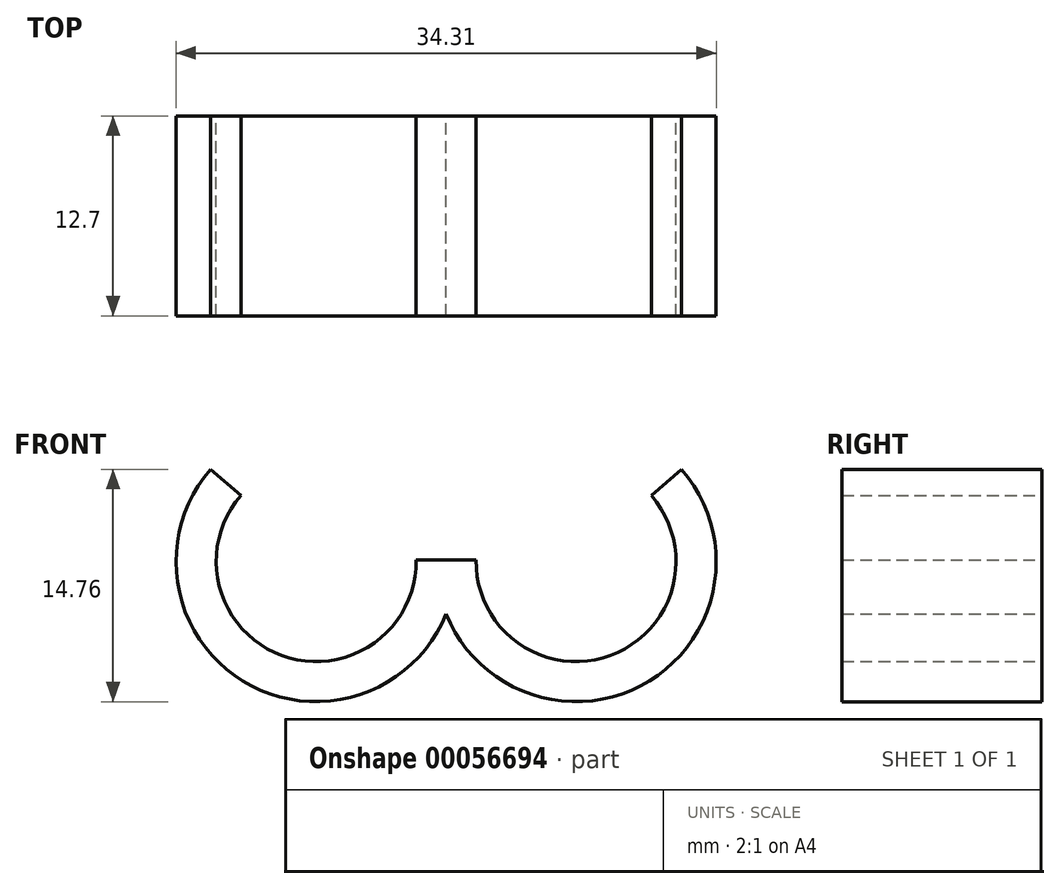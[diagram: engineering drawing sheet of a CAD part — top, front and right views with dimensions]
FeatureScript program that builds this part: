
annotation { "Feature Type Name" : "Feature", "Feature Type Description" : "" }
export const myFeature = defineFeature(function(context is Context, id is Id, definition is map)
    precondition{}
    {
        {
            var Q0;
            Q0=qCreatedBy(makeId("Front.planeOp"),FACE);
            var sketch = newSketch(context, id + "F0", { "sketchPlane" : qUnion([Q0])});
            skLineSegment(sketch, "E0", {"start": v(-28.08, 11.24) * mm, "end": v(-26.18, 11.24) * mm});
            skLineSegment(sketch, "E1", {"start": v(-26.18, 11.24) * mm, "end": v(-26.18, 15.94) * mm, "construction": true});
            skArc(sketch, "E2", {"start": v(-39.2, 15.32) * mm, "mid": v(-36.62, 5.18) * mm, "end": v(-28.08, 11.24) * mm});
            skLineSegment(sketch, "E3.MirrorCS", {"start": v(-24.27, 11.24) * mm, "end": v(-26.18, 11.24) * mm});
            skArc(sketch, "E4.MirrorCS", {"start": v(-13.15, 15.32) * mm, "mid": v(-15.74, 5.18) * mm, "end": v(-24.27, 11.24) * mm});
            skArc(sketch, "E5.0", {"start": v(-41.13, 17) * mm, "mid": v(-39.1, 3.56) * mm, "end": v(-26.18, 7.81) * mm});
            skArc(sketch, "E5.1", {"start": v(-11.23, 17) * mm, "mid": v(-13.26, 3.56) * mm, "end": v(-26.18, 7.81) * mm});
            skLineSegment(sketch, "E6", {"start": v(-41.13, 17) * mm, "end": v(-39.2, 15.32) * mm});
            skLineSegment(sketch, "E7", {"start": v(-13.15, 15.32) * mm, "end": v(-11.23, 17) * mm});
            skSolve(sketch);
        }
        {
            var Q0;
            Q0=makeQuery(id+"F0.imprint","IMPRINT",FACE,{"disambiguationData":[TD([[makeQuery(id+"F0.imprint","IMPRINT",EDGE,{"derivedFrom":sQuery(id+"F0.wireOp",EDGE,"E0")}),-1.0]])]});
            extrude(context, id + "F1", {"entities" : qUnion([Q0]), "depth" : 12.7 * mm});
        }
    });
